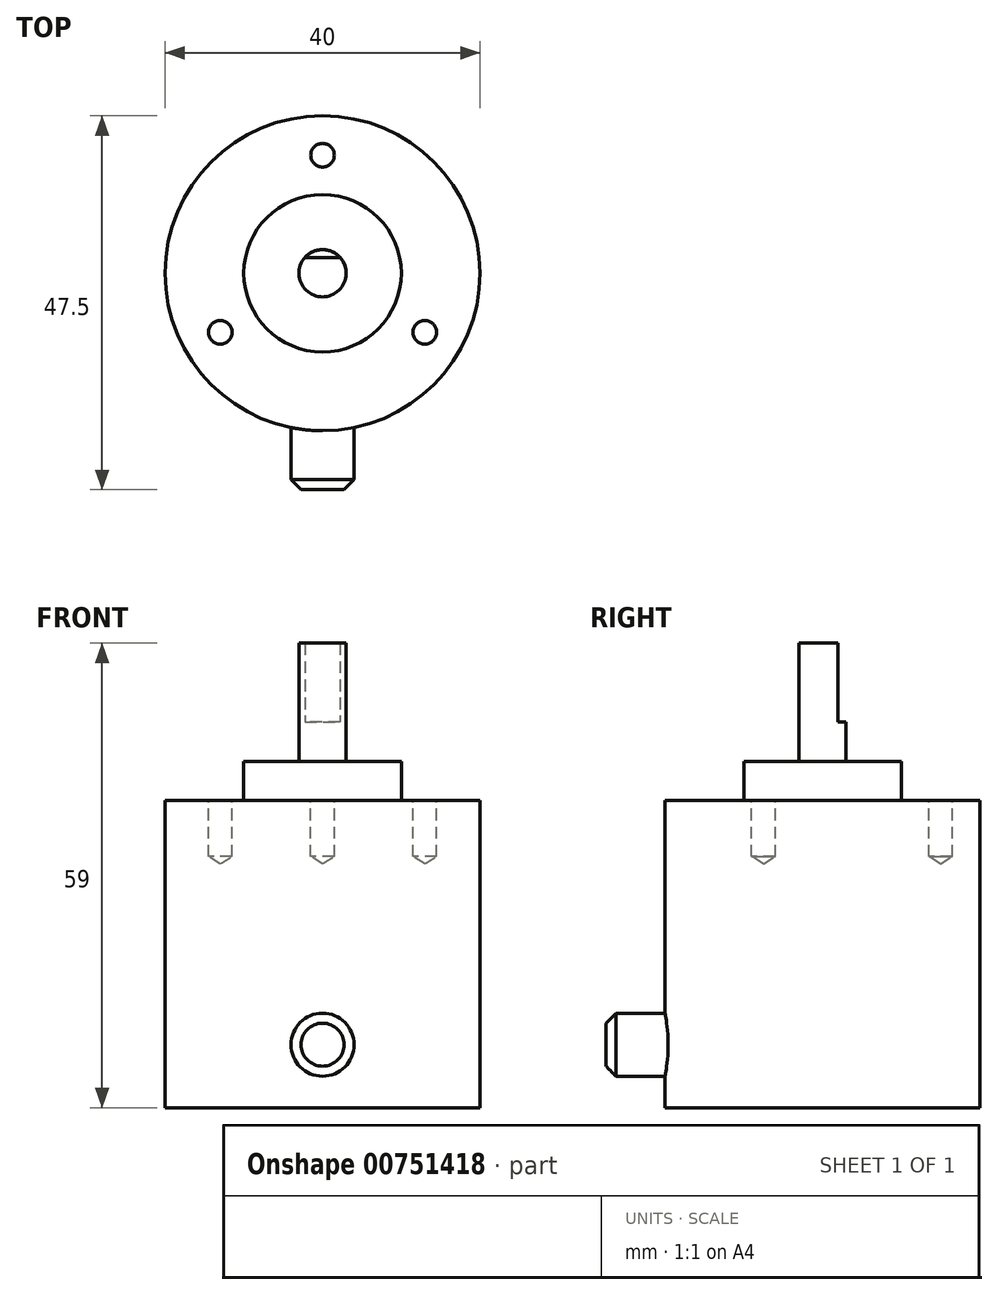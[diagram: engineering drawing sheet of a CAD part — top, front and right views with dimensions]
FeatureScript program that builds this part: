
annotation { "Feature Type Name" : "Feature", "Feature Type Description" : "" }
export const myFeature = defineFeature(function(context is Context, id is Id, definition is map)
    precondition{}
    {
        {
            var Q0;
            Q0=qCreatedBy(makeId("Top.planeOp"),FACE);
            var sketch = newSketch(context, id + "F0", { "sketchPlane" : qUnion([Q0])});
            skCircle(sketch, "E0", {"center": v(0, 0) * mm, "radius": 20 * mm});
            skCircle(sketch, "E1", {"center": v(0, 0) * mm, "radius": 10 * mm});
            skCircle(sketch, "E2", {"center": v(0, 0) * mm, "radius": 3 * mm});
            skLineSegment(sketch, "E3", {"start": v(-2.24, 2) * mm, "end": v(2.24, 2) * mm});
            skSolve(sketch);
        }
        {
            var Q0;
            Q0=makeQuery(id+"F0.imprint","IMPRINT",FACE,{"disambiguationData":[TD([[makeQuery(id+"F0.imprint","IMPRINT",EDGE,{"derivedFrom":sQuery(id+"F0.wireOp",EDGE,"E0")}),1.0]])]});
            extrude(context, id + "F1", {"entities" : qUnion([Q0]), "depth" : 39 * mm, "offsetDistance" : 25.4 * mm});
        }
        {
            var Q0;
            Q0=makeQuery(id+"F0.imprint","IMPRINT",FACE,{"disambiguationData":[TD([[makeQuery(id+"F0.imprint","IMPRINT",EDGE,{"derivedFrom":sQuery(id+"F0.wireOp",EDGE,"E1")}),1.0]])]});
            extrude(context, id + "F2", {"entities" : qUnion([Q0]), "operationType" : NewBodyOperationType.ADD, "depth" : 44 * mm, "offsetDistance" : 25.4 * mm});
        }
        {
            var Q0;
            {var subQ0=sQuery(id+"F0.wireOp",EDGE,"E3");Q0=makeQuery(id+"F0.imprint","IMPRINT",FACE,{"disambiguationData":[TD([[makeQuery(id+"F0.imprint","IMPRINT",EDGE,{"derivedFrom":subQ0}),-1.0]])]});}
            extrude(context, id + "F3", {"entities" : qUnion([Q0]), "operationType" : NewBodyOperationType.ADD, "depth" : 59 * mm, "offsetDistance" : 25.4 * mm});
        }
        {
            var Q0;
            {var subQ0=sQuery(id+"F0.wireOp",EDGE,"E3");Q0=makeQuery(id+"F0.imprint","IMPRINT",FACE,{"disambiguationData":[TD([[makeQuery(id+"F0.imprint","IMPRINT",EDGE,{"derivedFrom":subQ0}),1.0]])]});}
            extrude(context, id + "F4", {"entities" : qUnion([Q0]), "operationType" : NewBodyOperationType.ADD, "depth" : 49 * mm, "offsetDistance" : 25.4 * mm});
        }
        {
            var Q0;
            Q0=qCreatedBy(makeId("Front.planeOp"),FACE);
            cPlane(context, id + "F5", {"entities" : qUnion([Q0]), "cplaneType" : CPlaneType.OFFSET, "offset" : 20 * mm, "width" : 152.4 * mm, "height" : 152.4 * mm});
        }
        {
            var Q0;
            Q0=qCreatedBy(id+"F5.planeOp",FACE);
            var sketch = newSketch(context, id + "F6", { "sketchPlane" : qUnion([Q0])});
            skCircle(sketch, "E4", {"center": v(0, 8) * mm, "radius": 4 * mm});
            skSolve(sketch);
        }
        {
            var Q0;
            Q0=makeQuery(id+"F6.imprint","IMPRINT",FACE,{"disambiguationData":[TD([[makeQuery(id+"F6.imprint","IMPRINT",EDGE,{"derivedFrom":sQuery(id+"F6.wireOp",EDGE,"E4")}),1.0]])]});
            extrude(context, id + "F7", {"entities" : qUnion([Q0]), "operationType" : NewBodyOperationType.ADD, "depth" : 7.5 * mm, "offsetDistance" : 25.4 * mm, "hasSecondDirection" : true, "secondDirectionOppositeDirection" : true, "secondDirectionDepth" : 25.4 * mm});
        }
        {
            var Q0;
            Q0=makeQuery(id+"F7.opExtrude","CAP_EDGE",EDGE,{"disambiguationData":[OSD([sQuery(id+"F6.wireOp",EDGE,"E4")])],"isStart":false});
            chamfer(context, id + "F8", {"entities" : qUnion([Q0]), "width" : 1.27 * mm, "tangentPropagation" : true});
        }
        {
            var Q0;
            Q0=makeQuery(id+"F1.opExtrude","CAP_FACE",FACE,{"disambiguationData":[OSD([sQuery(id+"F0.wireOp",EDGE,"E0"),sQuery(id+"F0.wireOp",EDGE,"E1")])],"isStart":false});
            var sketch = newSketch(context, id + "F9", { "sketchPlane" : qUnion([Q0])});
            skCircle(sketch, "E5", {"center": v(0, 0) * mm, "radius": 15 * mm, "construction": true});
            skPoint(sketch, "E6", {"position": v(0, 15) * mm});
            skPoint(sketch, "E7", {"position": v(13, -7.5) * mm});
            skPoint(sketch, "E8", {"position": v(-13, -7.5) * mm});
            skLineSegment(sketch, "E9", {"start": v(0, 0) * mm, "end": v(0, 15) * mm, "construction": true});
            skLineSegment(sketch, "E10", {"start": v(0, 0) * mm, "end": v(13, -7.5) * mm, "construction": true});
            skLineSegment(sketch, "E11", {"start": v(-13, -7.5) * mm, "end": v(0, 0) * mm, "construction": true});
            skSolve(sketch);
        }
        {
            var Q0;
            Q0=sQuery(id+"F9.wireOp",VERTEX,"E6");
            var Q1;
            Q1=sQuery(id+"F9.wireOp",VERTEX,"E8");
            var Q2;
            Q2=sQuery(id+"F9.wireOp",VERTEX,"E7");
            var Q3;
            Q3=makeQuery(id+"F1.opExtrude","SWEPT_BODY",BODY,{"disambiguationData":[OSD([sQuery(id+"F0.wireOp",EDGE,"E0"),sQuery(id+"F0.wireOp",EDGE,"E1")])]});
            hole(context, id + "F10", {"style" : HoleStyle.SIMPLE, "endStyle" : HoleEndStyle.BLIND, "standardTappedOrClearance" : lookupTablePath({ "standard" : "ISO", "size" : "3", "type" : "Drilled" }), "standardBlindInLast" : lookupTablePath({ "standard" : "ISO", "size" : "3", "type" : "Drilled" }), "holeDiameter" : 3 * mm, "majorDiameter" : 6.35 * mm, "holeDepth" : 7.11 * mm, "isTappedThrough" : true, "tappedDepth" : 12.7 * mm, "tapClearance" : 3, "locations" : qUnion([Q0, Q1, Q2]), "scope" : qUnion([Q3])});
        }
    });
